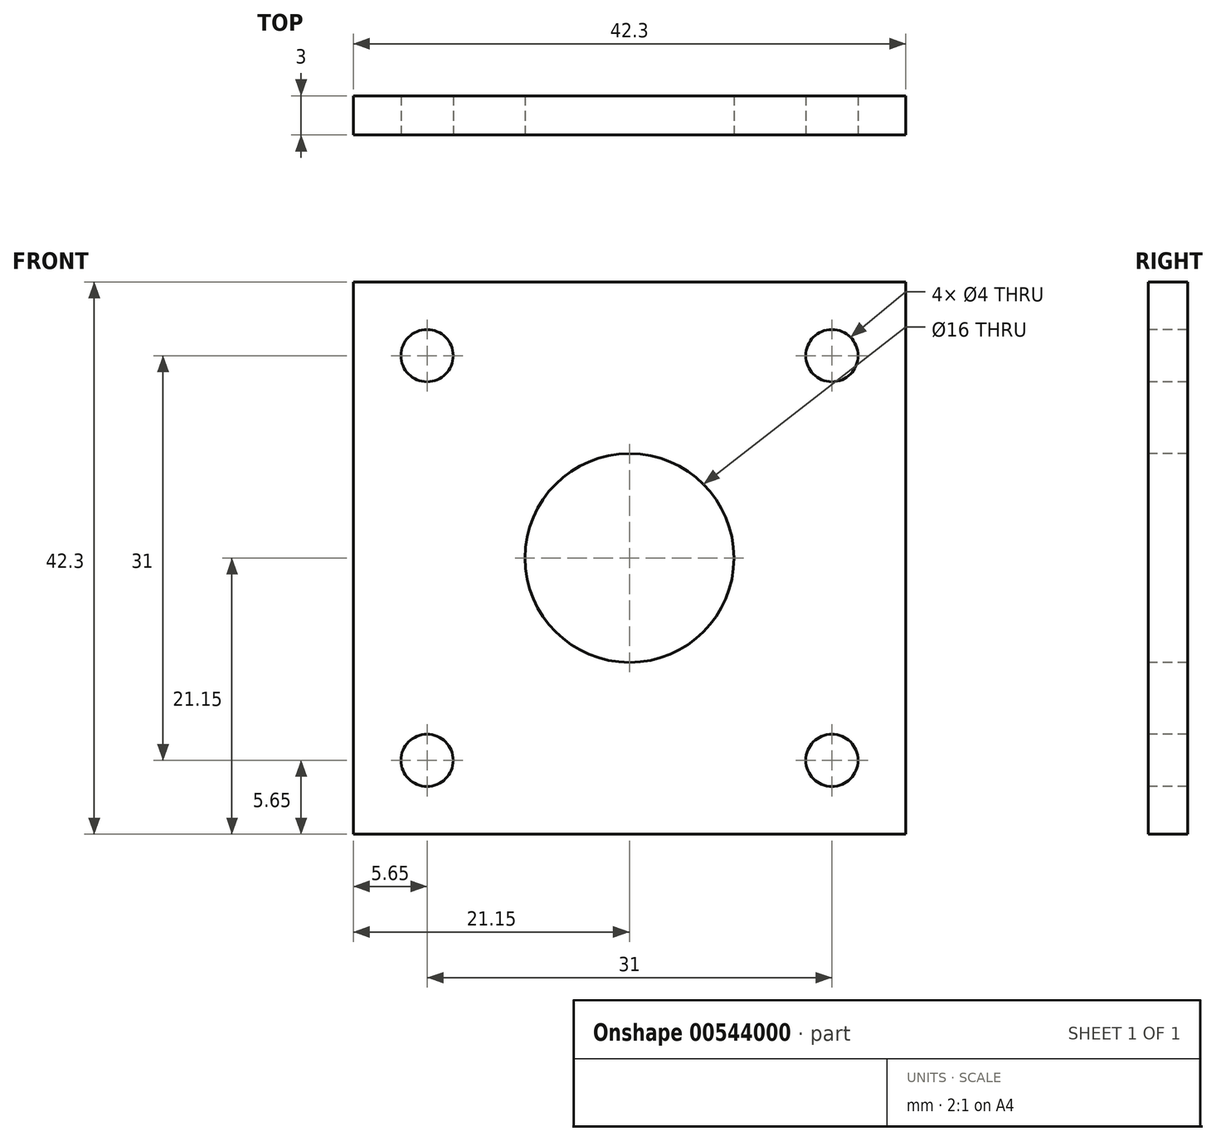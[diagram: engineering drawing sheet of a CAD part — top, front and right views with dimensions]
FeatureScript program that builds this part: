
annotation { "Feature Type Name" : "Feature", "Feature Type Description" : "" }
export const myFeature = defineFeature(function(context is Context, id is Id, definition is map)
    precondition{}
    {
        {
            var Q0;
            Q0=qCreatedBy(makeId("Front.planeOp"),FACE);
            var sketch = newSketch(context, id + "F0", { "sketchPlane" : qUnion([Q0])});
            skLineSegment(sketch, "E0.bottom", {"start": v(-21.15, 21.15) * mm, "end": v(21.15, 21.15) * mm});
            skLineSegment(sketch, "E0.top", {"start": v(-21.15, -21.15) * mm, "end": v(21.15, -21.15) * mm});
            skLineSegment(sketch, "E0.left", {"start": v(-21.15, 21.15) * mm, "end": v(-21.15, -21.15) * mm});
            skLineSegment(sketch, "E0.right", {"start": v(21.15, 21.15) * mm, "end": v(21.15, -21.15) * mm});
            skPoint(sketch, "E0.middle", {"position": v(0, 0) * mm});
            skLineSegment(sketch, "E1.bottom", {"start": v(15.5, 15.5) * mm, "end": v(-15.5, 15.5) * mm, "construction": true});
            skLineSegment(sketch, "E1.top", {"start": v(15.5, -15.5) * mm, "end": v(-15.5, -15.5) * mm, "construction": true});
            skLineSegment(sketch, "E1.left", {"start": v(15.5, 15.5) * mm, "end": v(15.5, -15.5) * mm, "construction": true});
            skLineSegment(sketch, "E1.right", {"start": v(-15.5, 15.5) * mm, "end": v(-15.5, -15.5) * mm, "construction": true});
            skSolve(sketch);
        }
        {
            var Q0;
            Q0 = qSketchRegion(id + "F0", true);
            extrude(context, id + "F1", {"entities" : qUnion([Q0]), "depth" : 3 * mm, "offsetDistance" : 25 * mm});
        }
        {
            var Q0;
            Q0=sQuery(id+"F0.wireOp",VERTEX,"E1.right.start");
            var Q1;
            Q1=sQuery(id+"F0.wireOp",VERTEX,"E1.left.start");
            var Q2;
            Q2=sQuery(id+"F0.wireOp",VERTEX,"E1.left.end");
            var Q3;
            Q3=sQuery(id+"F0.wireOp",VERTEX,"E1.right.end");
            var Q4;
            Q4=makeQuery(id+"F1.opExtrude","SWEPT_BODY",BODY,{"disambiguationData":[OSD([sQuery(id+"F0.wireOp",EDGE,"E0.bottom"),sQuery(id+"F0.wireOp",EDGE,"E0.top"),sQuery(id+"F0.wireOp",EDGE,"E0.left"),sQuery(id+"F0.wireOp",EDGE,"E0.right")])]});
            hole(context, id + "F2", {"style" : HoleStyle.SIMPLE, "endStyle" : HoleEndStyle.THROUGH, "oppositeDirection" : true, "holeDiameter" : 4 * mm, "majorDiameter" : 5 * mm, "isTappedThrough" : true, "tappedDepth" : 12 * mm, "tapClearance" : 3, "locations" : qUnion([Q0, Q1, Q2, Q3]), "scope" : qUnion([Q4])});
        }
        {
            var Q0;
            Q0=sQuery(id+"F0.wireOp",VERTEX,"E0.middle");
            var Q1;
            Q1=makeQuery(id+"F1.opExtrude","SWEPT_BODY",BODY,{"disambiguationData":[OSD([sQuery(id+"F0.wireOp",EDGE,"E0.bottom"),sQuery(id+"F0.wireOp",EDGE,"E0.top"),sQuery(id+"F0.wireOp",EDGE,"E0.left"),sQuery(id+"F0.wireOp",EDGE,"E0.right")])]});
            hole(context, id + "F3", {"style" : HoleStyle.SIMPLE, "endStyle" : HoleEndStyle.THROUGH, "oppositeDirection" : true, "holeDiameter" : 16 * mm, "majorDiameter" : 5 * mm, "isTappedThrough" : true, "tappedDepth" : 12 * mm, "tapClearance" : 3, "locations" : qUnion([Q0]), "scope" : qUnion([Q1])});
        }
    });
